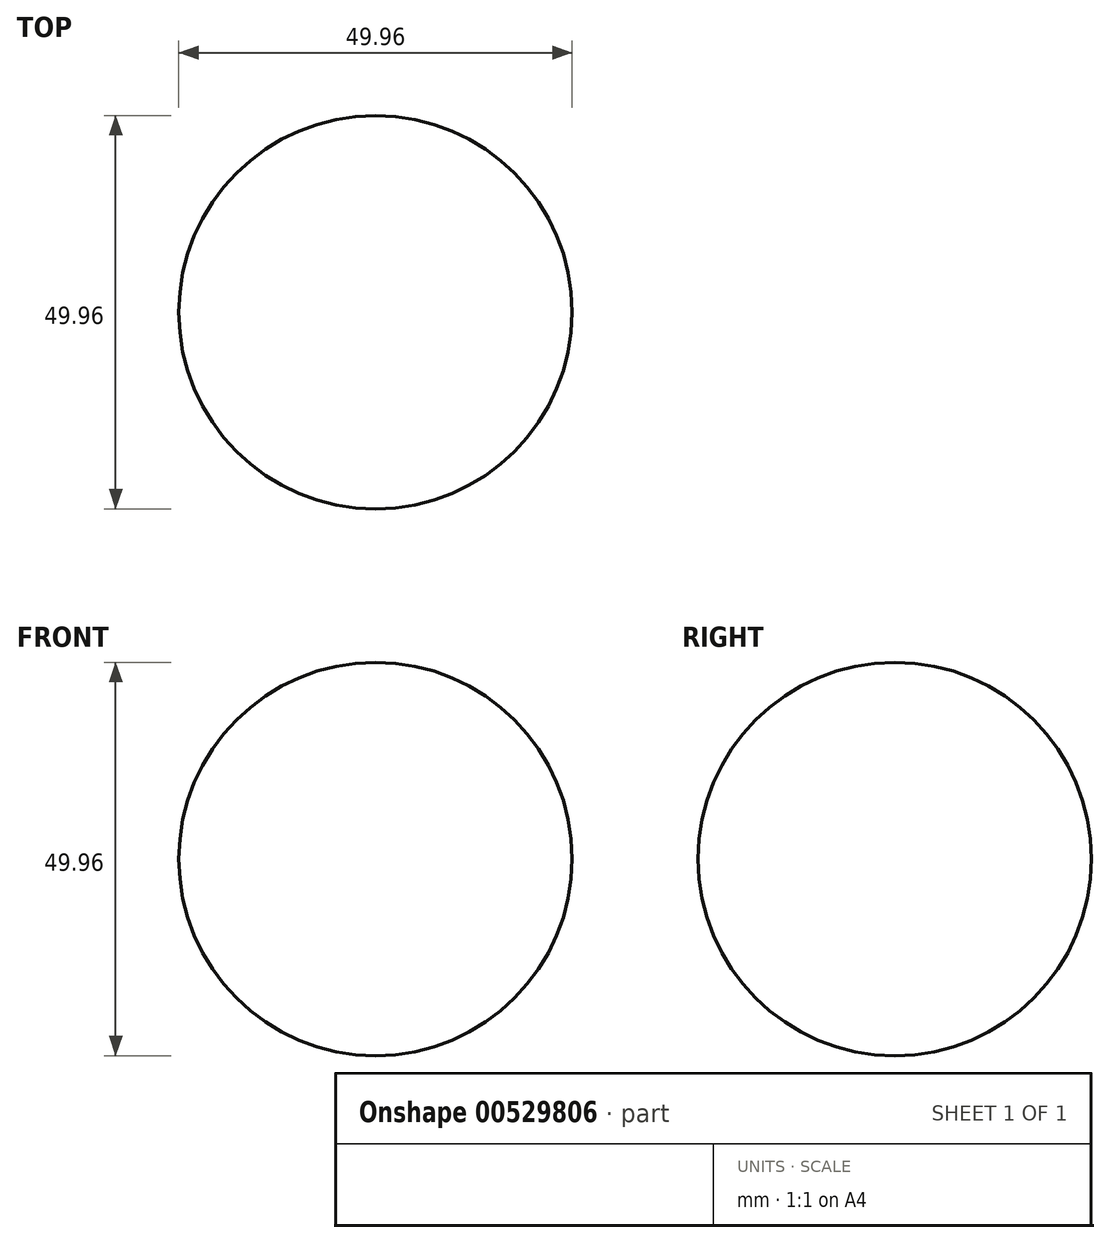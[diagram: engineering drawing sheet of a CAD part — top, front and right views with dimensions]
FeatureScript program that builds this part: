
annotation { "Feature Type Name" : "Feature", "Feature Type Description" : "" }
export const myFeature = defineFeature(function(context is Context, id is Id, definition is map)
    precondition{}
    {
        {
            var Q0;
            Q0=qCreatedBy(makeId("Top.planeOp"),FACE);
            var sketch = newSketch(context, id + "F0", { "sketchPlane" : qUnion([Q0])});
            skLineSegment(sketch, "E0", {"start": v(-23.59, 0) * mm, "end": v(26.37, 0) * mm});
            skArc(sketch, "E1", {"start": v(26.37, 0) * mm, "mid": v(1.4, 24.98) * mm, "end": v(-23.59, 0) * mm});
            skSolve(sketch);
        }
        {
            var Q0;
            Q0=makeQuery(id+"F0.imprint","IMPRINT",FACE,{"disambiguationData":[TD([[makeQuery(id+"F0.imprint","IMPRINT",EDGE,{"derivedFrom":sQuery(id+"F0.wireOp",EDGE,"E0")}),1.0]])]});
            var Q1;
            Q1=sQuery(id+"F0.wireOp",EDGE,"E0");
            revolve(context, id + "F1", {"entities" : qUnion([Q0]), "axis" : qUnion([Q1]), "revolveType" : RevolveType.FULL});
        }
    });
